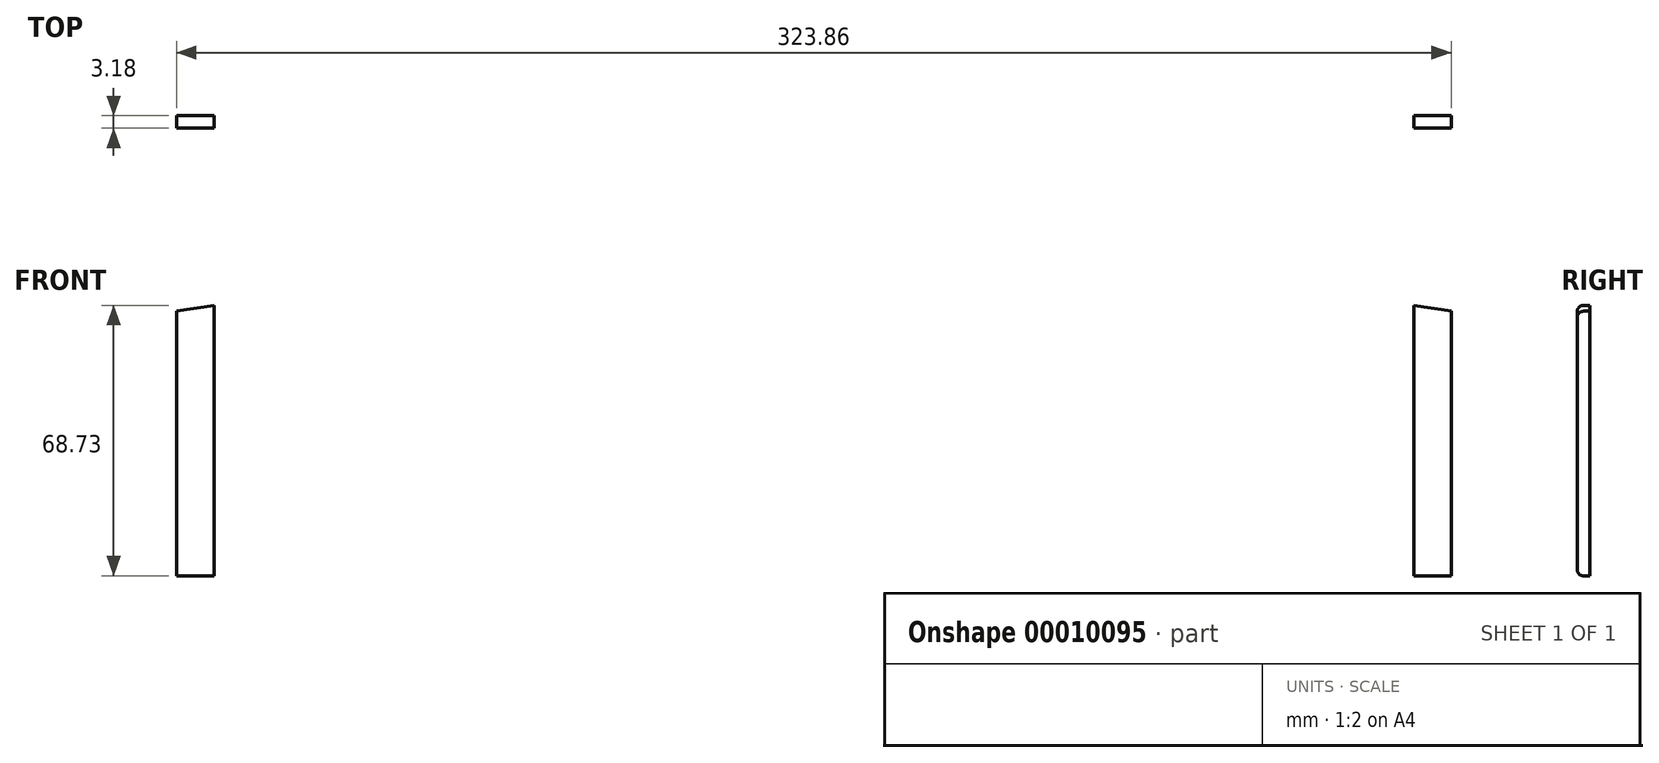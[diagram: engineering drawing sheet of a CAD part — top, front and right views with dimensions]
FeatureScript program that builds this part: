
annotation { "Feature Type Name" : "Feature", "Feature Type Description" : "" }
export const myFeature = defineFeature(function(context is Context, id is Id, definition is map)
    precondition{}
    {
        {
            var Q0;
            Q0=qCreatedBy(makeId("Front.planeOp"),FACE);
            var sketch = newSketch(context, id + "F0", { "sketchPlane" : qUnion([Q0])});
            skLineSegment(sketch, "E0.bottom", {"start": v(0, 0) * mm, "end": v(9.53, 0) * mm});
            skLineSegment(sketch, "E0.left", {"start": v(0, 0) * mm, "end": v(0, 68.73) * mm});
            skLineSegment(sketch, "E0.right", {"start": v(9.53, 0) * mm, "end": v(9.53, 67.22) * mm});
            skLineSegment(sketch, "E1", {"start": v(0, 68.73) * mm, "end": v(9.52, 67.22) * mm});
            skSolve(sketch);
        }
        {
            var Q0;
            Q0 = qSketchRegion(id + "F0", true);
            extrude(context, id + "F1", {"entities" : qUnion([Q0]), "endBound" : BoundingType.SYMMETRIC, "depth" : 3.17 * mm});
        }
        {
            var Q0;
            Q0=makeQuery(id+"F1.opExtrude","CAP_EDGE",EDGE,{"disambiguationData":[OSD([sQuery(id+"F0.wireOp",EDGE,"E1")])],"isStart":false});
            var Q1;
            Q1=makeQuery(id+"F1.opExtrude","CAP_EDGE",EDGE,{"disambiguationData":[OSD([sQuery(id+"F0.wireOp",EDGE,"E0.bottom")])],"isStart":false});
            fillet(context, id + "F2", {"entities" : qUnion([Q0, Q1]), "radius" : 1.59 * mm, "allowEdgeOverflow" : false});
        }
        {
            var Q0;
            Q0=qCreatedBy(makeId("Right.planeOp"),FACE);
            cPlane(context, id + "F3", {"entities" : qUnion([Q0]), "cplaneType" : CPlaneType.OFFSET, "offset" : 152.4 * mm, "oppositeDirection" : true, "width" : 152.4 * mm, "height" : 152.4 * mm});
        }
        {
            var Q0;
            Q0=makeQuery(id+"F1.opExtrude","SWEPT_BODY",BODY,{"disambiguationData":[OSD([sQuery(id+"F0.wireOp",EDGE,"E0.bottom"),sQuery(id+"F0.wireOp",EDGE,"E0.left"),sQuery(id+"F0.wireOp",EDGE,"E0.right"),sQuery(id+"F0.wireOp",EDGE,"E1")])]});
            var Q1;
            Q1=qCreatedBy(id+"F3.planeOp",FACE);
            mirror(context, id + "F4", {"entities" : qUnion([Q0]), "mirrorPlane" : qUnion([Q1])});
        }
    });
